# Revit family: АНТАРЕС_Воздушная завеса_1203AdWU
name_source: partatom
category: Оборудование
units: mm (PartAtom-declared; Revit-internal decimal feet)

## family parameters
Всегда вертикально = Да
Классификация = Нет
На основе рабочей плоскости = Нет
Общий = Нет
При загрузке вырезать с полостями = Нет
Размер круглого соединителя = Использовать диаметр
Тип детали = Нормальный
Точка расчета площади = Нет

## types (1)
- 1203AdWU
    ADSK_URL документации изделия = https://antar.ru
    ADSK_Единица измерения = шт.
    ADSK_Завод-изготовитель = ООО ''АНТАРЕС ПРО''
    ADSK_Количество = 1
    ADSK_Марка = 1203AdWU
    ADSK_Масса = 65
    ADSK_Материал = АНТАРЕС_Белый
    ADSK_Наименование = Завеса воздушная "АНТАРЕС" серия "Универсал-ПРО" модель 1203 АdWU
    ADSK_Напряжение = 380 В
    ADSK_Номинальная мощность = 750 Вт
    ADSK_Размер_Высота = 305 мм
    ADSK_Размер_Глубина = 528 мм
    ADSK_Размер_Ширина = 1170 мм
    ADSK_Расход жидкости = 0.3 л/с
    ADSK_Тепловая мощность = 30500 Вт
    D1 = 25 мм
    D2 = 25 мм
    URL = https://antar.ru
    Воздухопроизводительность = 4050.0 м³/ч
    Регулировка угла выдува воздушной струи (град.) = 0...+30
    Степень защиты = IP54
    Тип установки (горизонтальный / вертикальный) = Универсальный
    Уровень шума дБ(А) = 67
